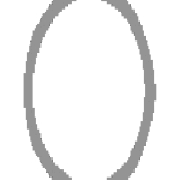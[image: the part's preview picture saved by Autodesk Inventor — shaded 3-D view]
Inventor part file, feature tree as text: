
AUTODESK INVENTOR PART (.ipt)
format: ipt  version: 2021 (Build 250183000, 183)  size: 110,080 bytes
history: native  units: in
note: dims shown in document units (in); Inventor stores cm internally (conversion verified against a paired STEP export)
features: other x4, sketch x3, plane x1
ambient origin geometry x8: Origin, YZ Plane, XZ Plane, XY Plane, X Axis, Y Axis, Z Axis, Center Point
bodies: Solid1 (feature_tree), Body (feature_tree)
feature tree (8):
  other  "Driven Length"
  other  "Frame Generator"
  other  "Start Plane"
  other  "End Plane"
  sketch  "Sketch"  dims[d2=13.5in d4=-0.0in d5=13.5in d6=0.12in d7=0.0in d8=90.0deg d9=13.5in]
  sketch  "Sketch2"  dims[d0=1.0in]
  plane  "Work Plane3"
  sketch  "Sketch3"  dims[d1=0.065in]
